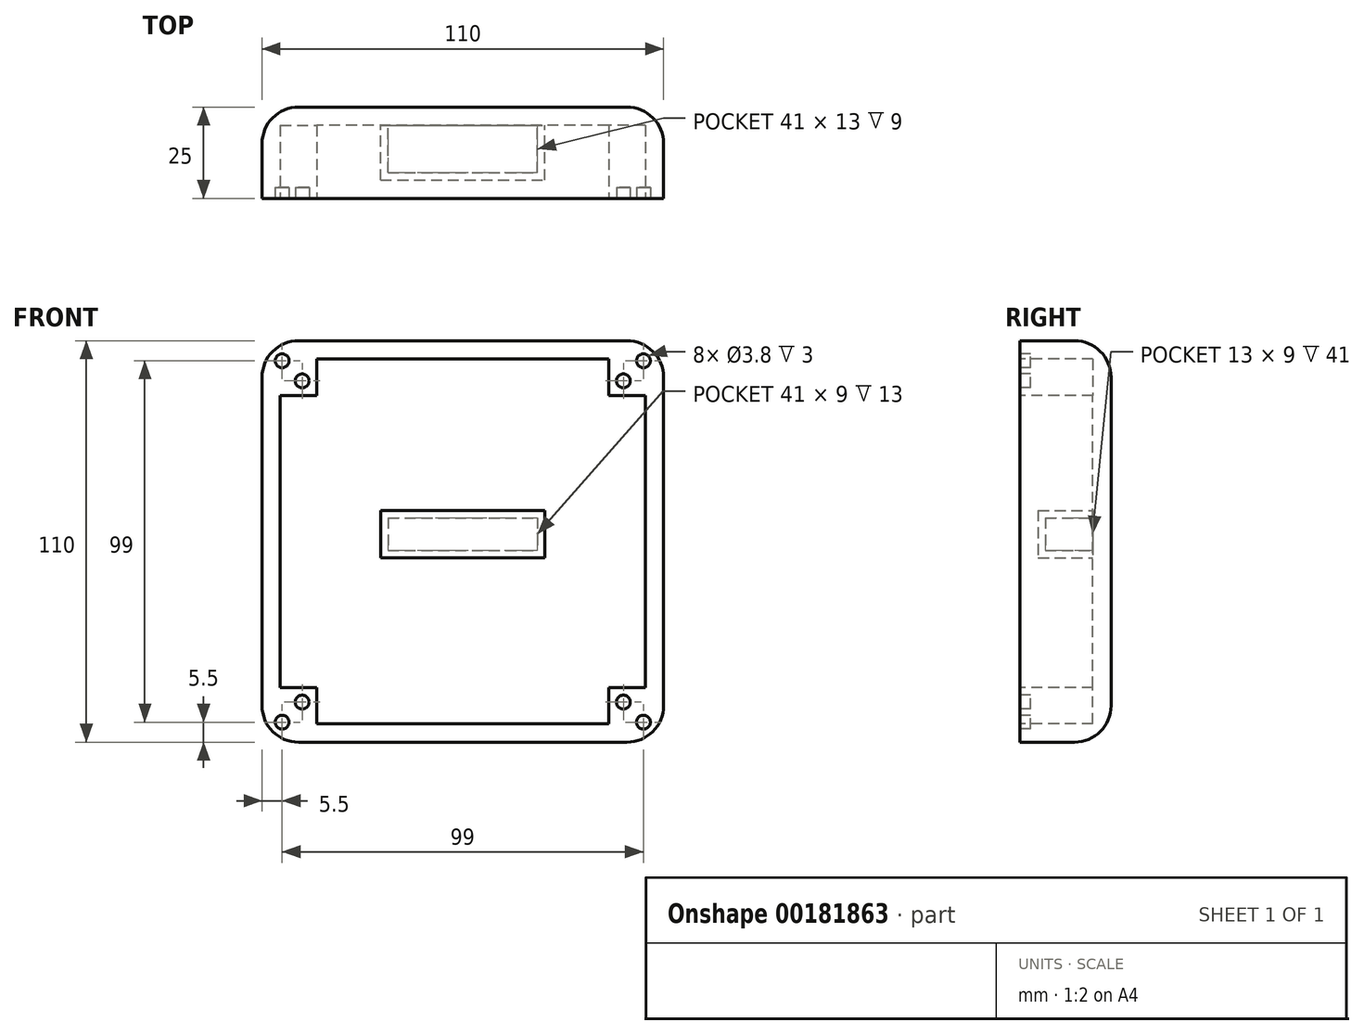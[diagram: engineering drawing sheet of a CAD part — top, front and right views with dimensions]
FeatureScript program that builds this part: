
annotation { "Feature Type Name" : "Feature", "Feature Type Description" : "" }
export const myFeature = defineFeature(function(context is Context, id is Id, definition is map)
    precondition{}
    {
        {
            var Q0;
            Q0=qCreatedBy(makeId("Front.planeOp"),FACE);
            var sketch = newSketch(context, id + "F0", { "sketchPlane" : qUnion([Q0])});
            skLineSegment(sketch, "E0.bottom", {"start": v(-55, 55) * mm, "end": v(55, 55) * mm});
            skLineSegment(sketch, "E0.top", {"start": v(-55, -55) * mm, "end": v(55, -55) * mm});
            skLineSegment(sketch, "E0.left", {"start": v(-55, 55) * mm, "end": v(-55, -55) * mm});
            skLineSegment(sketch, "E0.right", {"start": v(55, 55) * mm, "end": v(55, -55) * mm});
            skPoint(sketch, "E1", {"position": v(0, 55) * mm});
            skPoint(sketch, "E2", {"position": v(-55, 0) * mm});
            skPoint(sketch, "E3", {"position": v(55, 0) * mm});
            skPoint(sketch, "E4", {"position": v(0, -55) * mm});
            skSolve(sketch);
        }
        {
            var Q0;
            Q0 = qSketchRegion(id + "F0", true);
            extrude(context, id + "F1", {"entities" : qUnion([Q0]), "endBound" : BoundingType.SYMMETRIC, "depth" : 50 * mm});
        }
        {
            var Q0;
            Q0=makeQuery(id+"F1.opExtrude","CAP_FACE",FACE,{"disambiguationData":[OSD([sQuery(id+"F0.wireOp",EDGE,"E0.bottom"),sQuery(id+"F0.wireOp",EDGE,"E0.top"),sQuery(id+"F0.wireOp",EDGE,"E0.left"),sQuery(id+"F0.wireOp",EDGE,"E0.right")])],"isStart":false});
            var Q1;
            Q1=makeQuery(id+"F1.opExtrude","SWEPT_FACE",FACE,{"disambiguationData":[OSD([sQuery(id+"F0.wireOp",EDGE,"E0.right")])]});
            var Q2;
            Q2=makeQuery(id+"F1.opExtrude","SWEPT_FACE",FACE,{"disambiguationData":[OSD([sQuery(id+"F0.wireOp",EDGE,"E0.bottom")])]});
            var Q3;
            Q3=makeQuery(id+"F1.opExtrude","SWEPT_FACE",FACE,{"disambiguationData":[OSD([sQuery(id+"F0.wireOp",EDGE,"E0.left")])]});
            var Q4;
            Q4=makeQuery(id+"F1.opExtrude","SWEPT_FACE",FACE,{"disambiguationData":[OSD([sQuery(id+"F0.wireOp",EDGE,"E0.top")])]});
            fillet(context, id + "F2", {"entities" : qUnion([Q0, Q1, Q2, Q3, Q4]), "radius" : 10 * mm, "allowEdgeOverflow" : false});
        }
        {
            var Q0;
            Q0=qCreatedBy(makeId("Front.planeOp"),FACE);
            var sketch = newSketch(context, id + "F3", { "sketchPlane" : qUnion([Q0])});
            skLineSegment(sketch, "E5.bottom", {"start": v(55, 55) * mm, "end": v(-55, 55) * mm});
            skLineSegment(sketch, "E5.top", {"start": v(55, -55) * mm, "end": v(-55, -55) * mm});
            skLineSegment(sketch, "E5.left", {"start": v(-55, 55) * mm, "end": v(-55, -55) * mm});
            skLineSegment(sketch, "E5.right", {"start": v(55, 55) * mm, "end": v(55, -55) * mm});
            skPoint(sketch, "E6", {"position": v(0, 55) * mm});
            skPoint(sketch, "E7", {"position": v(-55, 0) * mm});
            skPoint(sketch, "E8", {"position": v(55, 0) * mm});
            skPoint(sketch, "E9", {"position": v(0, -55) * mm});
            skSolve(sketch);
        }
        {
            var Q0;
            Q0 = qSketchRegion(id + "F3", true);
            extrude(context, id + "F4", {"entities" : qUnion([Q0]), "operationType" : NewBodyOperationType.REMOVE, "depth" : 26 * mm});
        }
        {
            var Q0;
            Q0=qCreatedBy(makeId("Front.planeOp"),FACE);
            var sketch = newSketch(context, id + "F5", { "sketchPlane" : qUnion([Q0])});
            skLineSegment(sketch, "E10", {"start": v(40, 50) * mm, "end": v(-40, 50) * mm});
            skLineSegment(sketch, "E11", {"start": v(-40, 50) * mm, "end": v(-40, 40) * mm});
            skLineSegment(sketch, "E12", {"start": v(40, 50) * mm, "end": v(40, 40) * mm});
            skLineSegment(sketch, "E13", {"start": v(40, 40) * mm, "end": v(50, 40) * mm});
            skLineSegment(sketch, "E14", {"start": v(50, 40) * mm, "end": v(50, -40) * mm});
            skLineSegment(sketch, "E15", {"start": v(50, -40) * mm, "end": v(40, -40) * mm});
            skLineSegment(sketch, "E16", {"start": v(40, -40) * mm, "end": v(40, -50) * mm});
            skLineSegment(sketch, "E17", {"start": v(40, -50) * mm, "end": v(-40, -50) * mm});
            skLineSegment(sketch, "E18", {"start": v(-40, -50) * mm, "end": v(-40, -40) * mm});
            skLineSegment(sketch, "E19", {"start": v(-40, -40) * mm, "end": v(-50, -40) * mm});
            skLineSegment(sketch, "E20", {"start": v(-50, -40) * mm, "end": v(-50, 40) * mm});
            skLineSegment(sketch, "E21", {"start": v(-50, 40) * mm, "end": v(-40, 40) * mm});
            skPoint(sketch, "E22", {"position": v(55, 32.65) * mm});
            skSolve(sketch);
        }
        {
            var Q0;
            Q0 = qSketchRegion(id + "F5", true);
            extrude(context, id + "F6", {"entities" : qUnion([Q0]), "operationType" : NewBodyOperationType.REMOVE, "oppositeDirection" : true, "depth" : 20 * mm});
        }
        {
            var Q0;
            Q0=makeQuery(id+"F6.boolean.opBoolean","COPY",FACE,{"derivedFrom":makeQuery(id+"F6.opExtrude","CAP_FACE",FACE,{"disambiguationData":[OSD([sQuery(id+"F5.wireOp",EDGE,"E10"),sQuery(id+"F5.wireOp",EDGE,"E11"),sQuery(id+"F5.wireOp",EDGE,"E12"),sQuery(id+"F5.wireOp",EDGE,"E13"),sQuery(id+"F5.wireOp",EDGE,"E14"),sQuery(id+"F5.wireOp",EDGE,"E15"),sQuery(id+"F5.wireOp",EDGE,"E16"),sQuery(id+"F5.wireOp",EDGE,"E17"),sQuery(id+"F5.wireOp",EDGE,"E18"),sQuery(id+"F5.wireOp",EDGE,"E19"),sQuery(id+"F5.wireOp",EDGE,"E20"),sQuery(id+"F5.wireOp",EDGE,"E21")])],"isStart":false})});
            var sketch = newSketch(context, id + "F7", { "sketchPlane" : qUnion([Q0])});
            skLineSegment(sketch, "E23.bottom", {"start": v(-22.5, -4.5) * mm, "end": v(22.5, -4.5) * mm});
            skLineSegment(sketch, "E23.top", {"start": v(-22.5, 8.5) * mm, "end": v(22.5, 8.5) * mm});
            skLineSegment(sketch, "E23.left", {"start": v(-22.5, 8.5) * mm, "end": v(-22.5, -4.5) * mm});
            skLineSegment(sketch, "E23.right", {"start": v(22.5, 8.5) * mm, "end": v(22.5, -4.5) * mm});
            skPoint(sketch, "E24", {"position": v(22.5, 2) * mm});
            skPoint(sketch, "E25", {"position": v(0, 8.5) * mm});
            skLineSegment(sketch, "E26.bottom", {"start": v(-20.5, 6.5) * mm, "end": v(20.5, 6.5) * mm});
            skLineSegment(sketch, "E26.top", {"start": v(-20.5, -2.5) * mm, "end": v(20.5, -2.5) * mm});
            skLineSegment(sketch, "E26.left", {"start": v(-20.5, 6.5) * mm, "end": v(-20.5, -2.5) * mm});
            skLineSegment(sketch, "E26.right", {"start": v(20.5, 6.5) * mm, "end": v(20.5, -2.5) * mm});
            skSolve(sketch);
        }
        {
            var Q0;
            Q0 = qSketchRegion(id + "F7", true);
            extrude(context, id + "F8", {"entities" : qUnion([Q0]), "operationType" : NewBodyOperationType.ADD, "depth" : 15 * mm});
        }
        {
            var Q0;
            Q0=makeQuery(id+"F8.opExtrude","CAP_FACE",FACE,{"disambiguationData":[OSD([sQuery(id+"F7.wireOp",EDGE,"E23.bottom"),sQuery(id+"F7.wireOp",EDGE,"E23.top"),sQuery(id+"F7.wireOp",EDGE,"E23.left"),sQuery(id+"F7.wireOp",EDGE,"E23.right"),sQuery(id+"F7.wireOp",EDGE,"E26.bottom"),sQuery(id+"F7.wireOp",EDGE,"E26.top"),sQuery(id+"F7.wireOp",EDGE,"E26.left"),sQuery(id+"F7.wireOp",EDGE,"E26.right")])],"isStart":false});
            var sketch = newSketch(context, id + "F9", { "sketchPlane" : qUnion([Q0])});
            skLineSegment(sketch, "E27.bottom", {"start": v(-22.5, 8.5) * mm, "end": v(22.5, 8.5) * mm});
            skLineSegment(sketch, "E27.left", {"start": v(-22.5, 8.5) * mm, "end": v(-22.5, -4.5) * mm});
            skLineSegment(sketch, "E27.right", {"start": v(22.5, 8.5) * mm, "end": v(22.5, -4.5) * mm});
            skLineSegment(sketch, "E28", {"start": v(-22.5, -4.5) * mm, "end": v(22.5, -4.5) * mm});
            skSolve(sketch);
        }
        {
            var Q0;
            Q0 = qSketchRegion(id + "F9", true);
            extrude(context, id + "F10", {"entities" : qUnion([Q0]), "operationType" : NewBodyOperationType.ADD, "oppositeDirection" : true, "depth" : 2 * mm});
        }
        {
            var Q0;
            Q0=makeQuery(id+"F4.boolean.opBoolean","COPY",FACE,{"derivedFrom":makeQuery(id+"F4.opExtrude","CAP_FACE",FACE,{"disambiguationData":[OSD([sQuery(id+"F3.wireOp",EDGE,"E5.bottom"),sQuery(id+"F3.wireOp",EDGE,"E5.top"),sQuery(id+"F3.wireOp",EDGE,"E5.left"),sQuery(id+"F3.wireOp",EDGE,"E5.right")])],"isStart":true})});
            var sketch = newSketch(context, id + "F11", { "sketchPlane" : qUnion([Q0])});
            skCircle(sketch, "E29", {"center": v(49.5, 49.5) * mm, "radius": 1.9 * mm});
            skCircle(sketch, "E30", {"center": v(44, 44) * mm, "radius": 1.9 * mm});
            skCircle(sketch, "E31.MirrorC", {"center": v(-44, 44) * mm, "radius": 1.9 * mm});
            skCircle(sketch, "E32.MirrorC", {"center": v(-49.5, 49.5) * mm, "radius": 1.9 * mm});
            skCircle(sketch, "E33.MirrorC", {"center": v(-44, -44) * mm, "radius": 1.9 * mm});
            skCircle(sketch, "E34.MirrorC", {"center": v(-49.5, -49.5) * mm, "radius": 1.9 * mm});
            skCircle(sketch, "E35.MirrorC", {"center": v(44, -44) * mm, "radius": 1.9 * mm});
            skCircle(sketch, "E36.MirrorC", {"center": v(49.5, -49.5) * mm, "radius": 1.9 * mm});
            skPoint(sketch, "E37", {"position": v(-40, 50) * mm});
            skPoint(sketch, "E38", {"position": v(40, 50) * mm});
            skPoint(sketch, "E39", {"position": v(-50, 40) * mm});
            skPoint(sketch, "E40", {"position": v(50, 40) * mm});
            skSolve(sketch);
        }
        {
            var Q0;
            Q0 = qSketchRegion(id + "F11", true);
            extrude(context, id + "F12", {"entities" : qUnion([Q0]), "operationType" : NewBodyOperationType.REMOVE, "oppositeDirection" : true, "depth" : 3 * mm});
        }
    });
